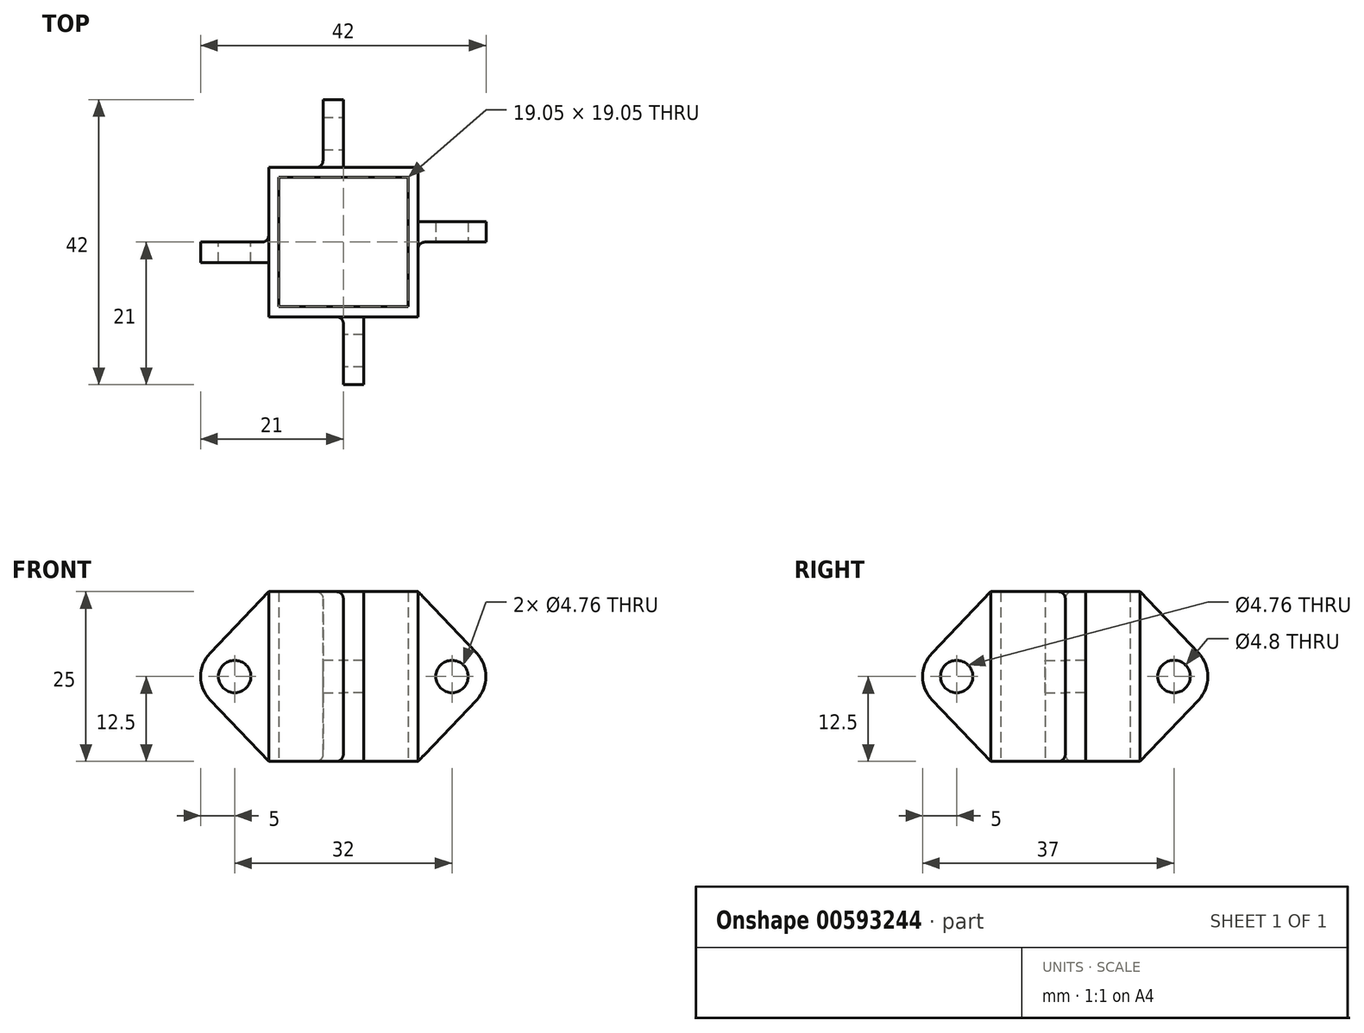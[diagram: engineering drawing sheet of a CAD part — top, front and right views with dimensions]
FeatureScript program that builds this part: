
annotation { "Feature Type Name" : "Feature", "Feature Type Description" : "" }
export const myFeature = defineFeature(function(context is Context, id is Id, definition is map)
    precondition{}
    {
        {
            var Q0;
            Q0=qCreatedBy(makeId("Top.planeOp"),FACE);
            var sketch = newSketch(context, id + "F0", { "sketchPlane" : qUnion([Q0])});
            skLineSegment(sketch, "E0.bottom", {"start": v(-9.53, 9.53) * mm, "end": v(9.53, 9.52) * mm});
            skLineSegment(sketch, "E0.top", {"start": v(-9.53, -9.52) * mm, "end": v(9.53, -9.53) * mm});
            skLineSegment(sketch, "E0.left", {"start": v(-9.52, 9.52) * mm, "end": v(-9.53, -9.52) * mm});
            skLineSegment(sketch, "E0.right", {"start": v(9.53, 9.52) * mm, "end": v(9.52, -9.52) * mm});
            skLineSegment(sketch, "E1.bottom", {"start": v(-11, 11) * mm, "end": v(11, 11) * mm});
            skLineSegment(sketch, "E1.top", {"start": v(-11, -11) * mm, "end": v(11, -11) * mm});
            skLineSegment(sketch, "E1.left", {"start": v(-11, 11) * mm, "end": v(-11, -11) * mm});
            skLineSegment(sketch, "E1.right", {"start": v(11, 11) * mm, "end": v(11, -11) * mm});
            skSolve(sketch);
        }
        {
            var Q0;
            Q0=qSketchRegion(id+"F0",true);
            extrude(context, id + "F1", {"entities" : qUnion([Q0]), "endBound" : BoundingType.SYMMETRIC, "depth" : 25 * mm});
        }
        {
            var Q0;
            Q0=qCreatedBy(makeId("Front.planeOp"),FACE);
            var sketch = newSketch(context, id + "F2", { "sketchPlane" : qUnion([Q0])});
            skCircle(sketch, "E2", {"center": v(-16, 0) * mm, "radius": 2.38 * mm});
            skLineSegment(sketch, "E3", {"start": v(-11, 12.5) * mm, "end": v(-19.62, 3.45) * mm});
            skLineSegment(sketch, "E4", {"start": v(-19.62, -3.45) * mm, "end": v(-11, -12.5) * mm});
            skArc(sketch, "E5", {"start": v(-19.62, 3.45) * mm, "mid": v(-21, 0) * mm, "end": v(-19.62, -3.45) * mm});
            skLineSegment(sketch, "E6", {"start": v(-11, 12.5) * mm, "end": v(-11, -12.5) * mm});
            skSolve(sketch);
        }
        {
            var Q0;
            Q0=qSketchRegion(id+"F2",true);
            extrude(context, id + "F3", {"entities" : qUnion([Q0]), "operationType" : NewBodyOperationType.ADD, "depth" : 3 * mm});
        }
        {
            var Q0;
            Q0=qCreatedBy(makeId("Right.planeOp"),FACE);
            var sketch = newSketch(context, id + "F4", { "sketchPlane" : qUnion([Q0])});
            skCircle(sketch, "E7", {"center": v(-16, 0) * mm, "radius": 2.38 * mm});
            skLineSegment(sketch, "E8", {"start": v(-19.62, 3.45) * mm, "end": v(-11, 12.5) * mm});
            skLineSegment(sketch, "E9.MirrorCS", {"start": v(-19.62, -3.45) * mm, "end": v(-11, -12.5) * mm});
            skLineSegment(sketch, "E10", {"start": v(-11, 12.5) * mm, "end": v(-11, -12.5) * mm});
            skArc(sketch, "E11", {"start": v(-19.62, 3.45) * mm, "mid": v(-21, 0) * mm, "end": v(-19.62, -3.45) * mm});
            skSolve(sketch);
        }
        {
            var Q0;
            Q0=qSketchRegion(id+"F4",true);
            extrude(context, id + "F5", {"entities" : qUnion([Q0]), "operationType" : NewBodyOperationType.ADD, "depth" : 3 * mm});
        }
        {
            var Q0;
            Q0=qCreatedBy(makeId("Front.planeOp"),FACE);
            var sketch = newSketch(context, id + "F6", { "sketchPlane" : qUnion([Q0])});
            skCircle(sketch, "E12", {"center": v(16, 0) * mm, "radius": 2.38 * mm});
            skLineSegment(sketch, "E13", {"start": v(19.62, -3.45) * mm, "end": v(11, -12.5) * mm});
            skLineSegment(sketch, "E14", {"start": v(11, 12.5) * mm, "end": v(19.62, 3.45) * mm});
            skLineSegment(sketch, "E15", {"start": v(11, -12.5) * mm, "end": v(11, 12.5) * mm});
            skArc(sketch, "E16", {"start": v(19.62, -3.45) * mm, "mid": v(21, 0) * mm, "end": v(19.62, 3.45) * mm});
            skSolve(sketch);
        }
        {
            var Q0;
            Q0=qSketchRegion(id+"F6",true);
            extrude(context, id + "F7", {"entities" : qUnion([Q0]), "operationType" : NewBodyOperationType.ADD, "oppositeDirection" : true, "depth" : 3 * mm});
        }
        {
            var Q0;
            Q0=qCreatedBy(makeId("Right.planeOp"),FACE);
            var sketch = newSketch(context, id + "F8", { "sketchPlane" : qUnion([Q0])});
            skCircle(sketch, "E17", {"center": v(16, 0) * mm, "radius": 2.4 * mm});
            skLineSegment(sketch, "E18", {"start": v(19.62, 3.45) * mm, "end": v(11, 12.5) * mm});
            skLineSegment(sketch, "E19", {"start": v(11, 12.5) * mm, "end": v(11, -12.5) * mm});
            skLineSegment(sketch, "E20", {"start": v(11, -12.5) * mm, "end": v(19.62, -3.45) * mm});
            skArc(sketch, "E21", {"start": v(19.62, -3.45) * mm, "mid": v(21, 0) * mm, "end": v(19.62, 3.45) * mm});
            skSolve(sketch);
        }
        {
            var Q0;
            Q0=qSketchRegion(id+"F8",true);
            extrude(context, id + "F9", {"entities" : qUnion([Q0]), "operationType" : NewBodyOperationType.ADD, "oppositeDirection" : true, "depth" : 3 * mm});
        }
        {
            var Q0;
            Q0=makeQuery(id+"F3.opExtrude","CAP_EDGE",EDGE,{"disambiguationData":[OSD([sQuery(id+"F2.wireOp",EDGE,"E6")])],"isStart":false});
            var Q1;
            Q1=makeQuery(id+"F5.opExtrude","CAP_EDGE",EDGE,{"disambiguationData":[OSD([sQuery(id+"F4.wireOp",EDGE,"E10")])],"isStart":true});
            var Q2;
            Q2=makeQuery(id+"F5.opExtrude","CAP_EDGE",EDGE,{"disambiguationData":[OSD([sQuery(id+"F4.wireOp",EDGE,"E10")])],"isStart":false});
            var Q3;
            Q3=makeQuery(id+"F3.opExtrude","CAP_EDGE",EDGE,{"disambiguationData":[OSD([sQuery(id+"F2.wireOp",EDGE,"5e426696-2d0d-4448-9194-7e160c71353e2.MirrorCS")])],"isStart":false});
            var Q4;
            Q4=makeQuery(id+"F3.opExtrude","CAP_EDGE",EDGE,{"disambiguationData":[OSD([sQuery(id+"F2.wireOp",EDGE,"5e426696-2d0d-4448-9194-7e160c71353e2.MirrorCS")])],"isStart":true});
            var Q5;
            Q5=makeQuery(id+"F5.opExtrude","CAP_EDGE",EDGE,{"disambiguationData":[OSD([sQuery(id+"F4.wireOp",EDGE,"1f8986f2-1053-424e-8057-c49cb6aa39cc2.MirrorCS")])],"isStart":false});
            var Q6;
            Q6=makeQuery(id+"F3.opExtrude","CAP_EDGE",EDGE,{"disambiguationData":[OSD([sQuery(id+"F2.wireOp",EDGE,"E6")])],"isStart":true});
            var Q7;
            Q7=makeQuery(id+"F5.opExtrude","CAP_EDGE",EDGE,{"disambiguationData":[OSD([sQuery(id+"F4.wireOp",EDGE,"1f8986f2-1053-424e-8057-c49cb6aa39cc2.MirrorCS")])],"isStart":true});
            var Q8;
            Q8=makeQuery(id+"F7.opExtrude","CAP_EDGE",EDGE,{"disambiguationData":[OSD([sQuery(id+"F6.wireOp",EDGE,"E15")])],"isStart":true});
            var Q9;
            Q9=makeQuery(id+"F7.opExtrude","CAP_EDGE",EDGE,{"disambiguationData":[OSD([sQuery(id+"F6.wireOp",EDGE,"E15")])],"isStart":false});
            var Q10;
            Q10=makeQuery(id+"F9.opExtrude","CAP_EDGE",EDGE,{"disambiguationData":[OSD([sQuery(id+"F8.wireOp",EDGE,"E19")])],"isStart":true});
            var Q11;
            Q11=makeQuery(id+"F9.opExtrude","CAP_EDGE",EDGE,{"disambiguationData":[OSD([sQuery(id+"F8.wireOp",EDGE,"E19")])],"isStart":false});
            fillet(context, id + "F10", {"entities" : qUnion([Q0, Q1, Q2, Q3, Q4, Q5, Q6, Q7, Q8, Q9, Q10, Q11]), "radius" : 1 * mm, "tangentPropagation" : true, "allowEdgeOverflow" : false});
        }
    });
